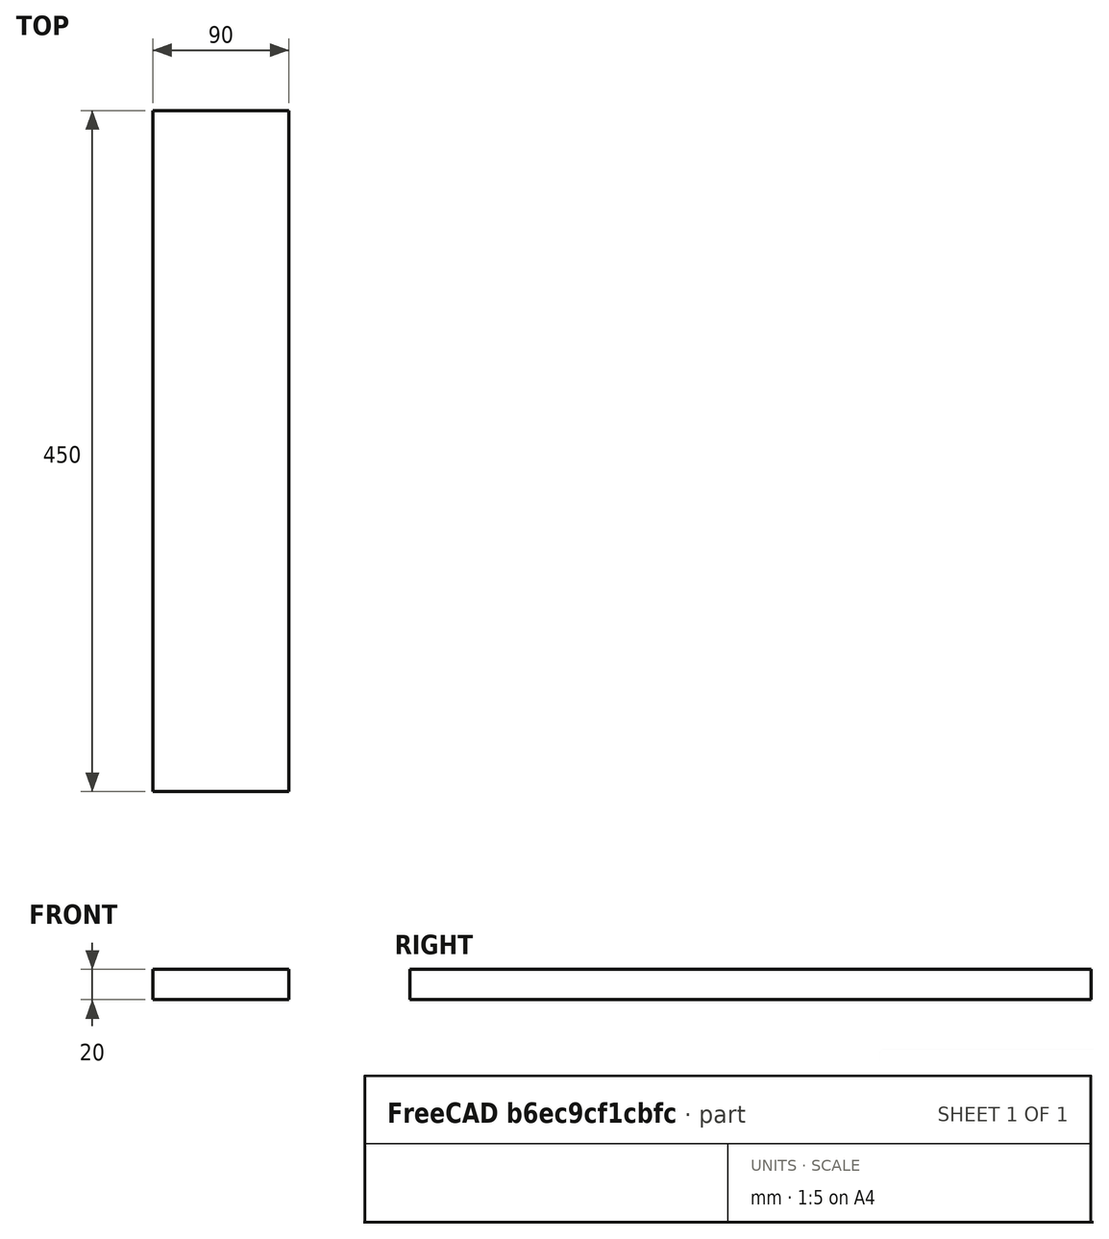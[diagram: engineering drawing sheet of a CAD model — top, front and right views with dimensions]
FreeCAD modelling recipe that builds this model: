
FCSTD DOCUMENT  (FreeCAD 0.20R29603 (Git))
Label: RadkastenOben
License: All rights reserved
LicenseURL: http://en.wikipedia.org/wiki/All_rights_reserved
objects: Sketcher::SketchObject×1, PartDesign::Pad×1, PartDesign::Body×1
note: 4 computed .brp shape members not serialized (recipe doc carries the construction recipe); baked Part::Feature solids carry a one-line shape summary decoded from their .brp

FEATURE [Sketcher::SketchObject] Sketch
  FullyConstrained = true
  MapMode = 5
  Support = -> [XY_Plane]
  sketch-geometry (4):
    g0: LineSegment StartX=0 StartY=0 StartZ=0 EndX=-90 EndY=0 EndZ=0
    g1: LineSegment StartX=-90 StartY=0 StartZ=0 EndX=-90 EndY=450 EndZ=0
    g2: LineSegment StartX=-90 StartY=450 StartZ=0 EndX=0 EndY=450 EndZ=0
    g3: LineSegment StartX=0 StartY=450 StartZ=0 EndX=0 EndY=0 EndZ=0
  constraints (11):
    c: Coincident(g0,g1)
    c: Coincident(g1,g2)
    c: Coincident(g2,g3)
    c: Coincident(g3,g0)
    c: Horizontal(g0)
    c: Horizontal(g2)
    c: Vertical(g1)
    c: Vertical(g3)
    c: Coincident(g0,g-1)
    c: Distance(g2) = 90
    c: Distance(g3) = 450
FEATURE [PartDesign::Pad] Pad
  Direction = (0,0,1)
  Length = 20
  Length2 = 10
  Profile = -> Sketch
  ReferenceAxis = -> Sketch [N_Axis]
  Type = 0
FEATURE [PartDesign::Body] Body
  Group = -> [Sketch,Pad]
  Origin = -> Origin
  Tip = -> Pad
